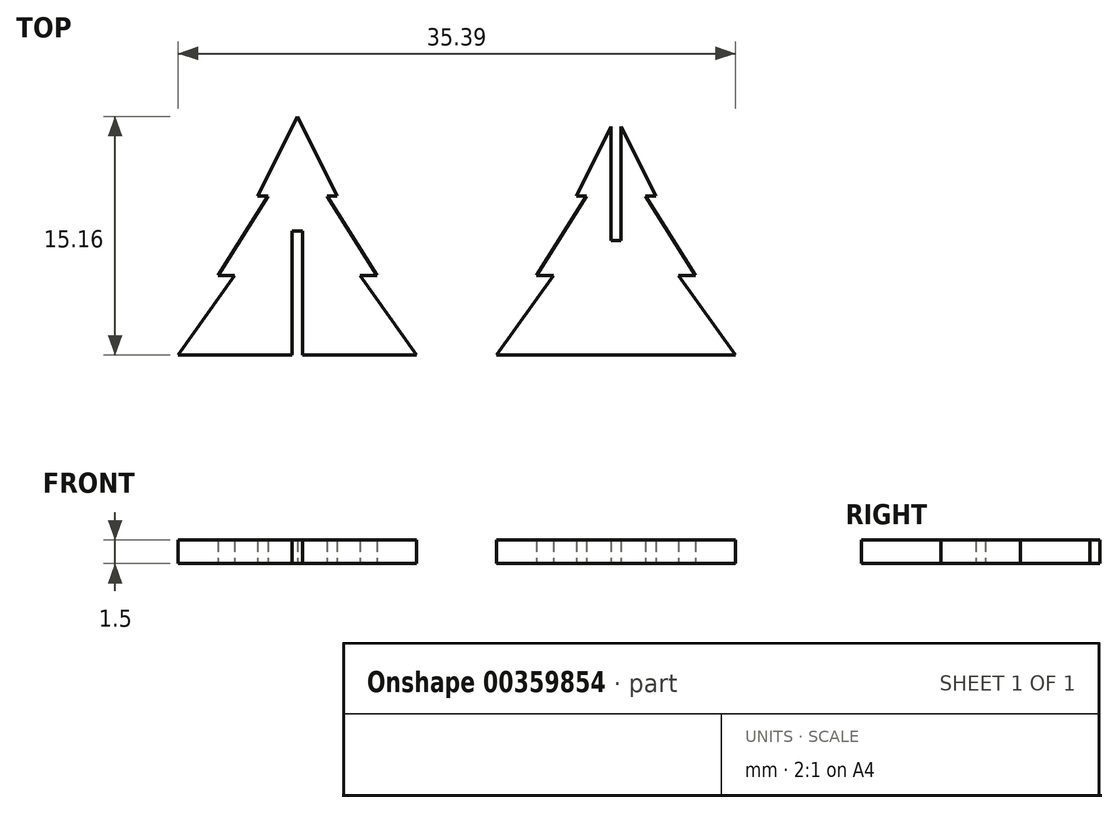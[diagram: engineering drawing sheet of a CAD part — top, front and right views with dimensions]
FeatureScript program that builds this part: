
annotation { "Feature Type Name" : "Feature", "Feature Type Description" : "" }
export const myFeature = defineFeature(function(context is Context, id is Id, definition is map)
    precondition{}
    {
        {
            var Q0;
            Q0=qCreatedBy(makeId("Top.planeOp"),FACE);
            var sketch = newSketch(context, id + "F0", { "sketchPlane" : qUnion([Q0])});
            skLineSegment(sketch, "E0", {"start": v(7.58, 0) * mm, "end": v(3.98, 5.05) * mm});
            skLineSegment(sketch, "E1", {"start": v(3.98, 5.05) * mm, "end": v(5.05, 5.05) * mm});
            skLineSegment(sketch, "E2", {"start": v(5.05, 5.05) * mm, "end": v(1.88, 10.1) * mm});
            skLineSegment(sketch, "E3", {"start": v(1.88, 10.1) * mm, "end": v(2.53, 10.1) * mm});
            skLineSegment(sketch, "E4", {"start": v(0, 0) * mm, "end": v(7.58, 0) * mm});
            skLineSegment(sketch, "E5.MirrorCS", {"start": v(-5.05, 5.05) * mm, "end": v(-1.88, 10.1) * mm});
            skLineSegment(sketch, "E6.MirrorCS", {"start": v(-7.58, 0) * mm, "end": v(-3.98, 5.05) * mm});
            skLineSegment(sketch, "E7.MirrorCS", {"start": v(0, 0) * mm, "end": v(-7.58, 0) * mm});
            skLineSegment(sketch, "E8.MirrorCS", {"start": v(-1.88, 10.1) * mm, "end": v(-2.53, 10.1) * mm});
            skLineSegment(sketch, "E9.MirrorCS", {"start": v(-3.98, 5.05) * mm, "end": v(-5.05, 5.05) * mm});
            skLineSegment(sketch, "E10", {"start": v(-10.12, 18.88) * mm, "end": v(-10.12, 0) * mm, "construction": true});
            skLineSegment(sketch, "E11.MirrorCS", {"start": v(-17.7, 10.1) * mm, "end": v(-20.23, 15.16) * mm});
            skLineSegment(sketch, "E12.MirrorCS", {"start": v(-22.76, 10.1) * mm, "end": v(-20.23, 15.16) * mm});
            skLineSegment(sketch, "E13.MirrorCS", {"start": v(-15.18, 5.05) * mm, "end": v(-18.36, 10.1) * mm});
            skLineSegment(sketch, "E14.MirrorCS", {"start": v(-25.29, 5.05) * mm, "end": v(-22.11, 10.1) * mm});
            skLineSegment(sketch, "E15.MirrorCS", {"start": v(-12.66, 0) * mm, "end": v(-16.26, 5.05) * mm});
            skLineSegment(sketch, "E16.MirrorCS", {"start": v(-27.81, 0) * mm, "end": v(-24.21, 5.05) * mm});
            skLineSegment(sketch, "E17.MirrorCS", {"start": v(-16.26, 5.05) * mm, "end": v(-15.18, 5.05) * mm});
            skLineSegment(sketch, "E18.MirrorCS", {"start": v(-24.21, 5.05) * mm, "end": v(-25.29, 5.05) * mm});
            skLineSegment(sketch, "E19.MirrorCS", {"start": v(-18.36, 10.1) * mm, "end": v(-17.7, 10.1) * mm});
            skLineSegment(sketch, "E20.MirrorCS", {"start": v(-22.11, 10.1) * mm, "end": v(-22.76, 10.1) * mm});
            skLineSegment(sketch, "E21", {"start": v(-0.33, 7.58) * mm, "end": v(-0.33, 8.51) * mm, "construction": true});
            skLineSegment(sketch, "E22", {"start": v(-0.33, 7.58) * mm, "end": v(-0.33, 14.5) * mm});
            skLineSegment(sketch, "E23.MirrorCS", {"start": v(0.33, 7.58) * mm, "end": v(0.33, 14.5) * mm});
            skLineSegment(sketch, "E24", {"start": v(0.33, 14.5) * mm, "end": v(2.53, 10.1) * mm});
            skLineSegment(sketch, "E25", {"start": v(-0.33, 14.5) * mm, "end": v(-2.53, 10.1) * mm});
            skLineSegment(sketch, "E26.MirrorCS", {"start": v(-20.56, 7.58) * mm, "end": v(-20.56, 0.65) * mm});
            skLineSegment(sketch, "E27.MirrorCS", {"start": v(-19.9, 7.58) * mm, "end": v(-19.9, 0.65) * mm});
            skLineSegment(sketch, "E28", {"start": v(-19.9, 0.65) * mm, "end": v(-19.9, 0) * mm});
            skLineSegment(sketch, "E29", {"start": v(-20.56, 0.65) * mm, "end": v(-20.56, 0) * mm});
            skLineSegment(sketch, "E30", {"start": v(-27.81, 0) * mm, "end": v(-20.56, 0) * mm});
            skLineSegment(sketch, "E31", {"start": v(-19.9, 0) * mm, "end": v(-12.66, 0) * mm});
            skLineSegment(sketch, "E32", {"start": v(-20.56, 7.88) * mm, "end": v(-19.9, 7.88) * mm});
            skLineSegment(sketch, "E33", {"start": v(-19.9, 7.88) * mm, "end": v(-19.9, 7.58) * mm});
            skLineSegment(sketch, "E34", {"start": v(-20.56, 7.88) * mm, "end": v(-20.56, 7.58) * mm});
            skLineSegment(sketch, "E35", {"start": v(-0.33, 7.28) * mm, "end": v(0.33, 7.28) * mm});
            skLineSegment(sketch, "E36", {"start": v(0.33, 7.28) * mm, "end": v(0.33, 7.58) * mm});
            skLineSegment(sketch, "E37", {"start": v(-0.33, 7.28) * mm, "end": v(-0.33, 7.58) * mm});
            skSolve(sketch);
        }
        {
            var Q0;
            Q0=makeQuery(id+"F0.imprint","IMPRINT",FACE,{"disambiguationData":[TD([[makeQuery(id+"F0.imprint","IMPRINT",EDGE,{"derivedFrom":sQuery(id+"F0.wireOp",EDGE,"E11.MirrorCS")}),1.0]])]});
            var Q1;
            Q1=makeQuery(id+"F0.imprint","IMPRINT",FACE,{"disambiguationData":[TD([[makeQuery(id+"F0.imprint","IMPRINT",EDGE,{"derivedFrom":sQuery(id+"F0.wireOp",EDGE,"E0")}),1.0]])]});
            extrude(context, id + "F1", {"entities" : qUnion([Q0, Q1]), "depth" : 1.5 * mm});
        }
    });
